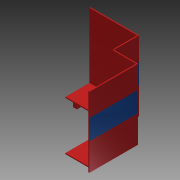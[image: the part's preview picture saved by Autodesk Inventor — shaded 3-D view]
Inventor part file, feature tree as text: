
AUTODESK INVENTOR PART (.ipt)
format: ipt  version: 2014 (Build 180170000, 170)  size: 247,296 bytes
history: native  units: in
note: dims shown in document units (in); Inventor stores cm internally (conversion verified against a paired STEP export)
features: extrude x16, sketch x16
ambient origin geometry x8: Origin, YZ Plane, XZ Plane, XY Plane, X Axis, Y Axis, Z Axis, Center Point
bodies: Solid1 (feature_tree)
feature tree (32):
  extrude  "Extrusion1"  Depth=23.5in
  extrude  "Extrusion2"  Depth=47.5in
  extrude  "Extrusion3"  Depth=64.5in
  extrude  "Extrusion4"  Depth=64.5in
  extrude  "Extrusion5"  Depth=1.0in TaperAngle=0.0deg
  extrude  "Extrusion6"  Depth=1.0in TaperAngle=0.0deg
  extrude  "Extrusion7"  Depth=4.0in
  extrude  "Extrusion8"  Depth=4.0in TaperAngle=0.0deg
  extrude  "Extrusion9"  Depth=4.0in
  extrude  "Extrusion10"  Depth=1.0in TaperAngle=0.0deg
  extrude  "Extrusion11"  Depth=1.0in TaperAngle=0.0deg
  extrude  "Extrusion12"  Depth=1.0in TaperAngle=0.0deg
  sketch  "Sketch13"  dims[d36=0.0in d37=0.0in d38=0.0in d39=0.0in]
  sketch  "Sketch14"  dims[d40=0.0in d41=0.0in d42=0.0in d43=0.0in]
  sketch  "Sketch15"
  sketch  "Sketch16"
  extrude  "Extrusion13"  Depth=0.0in TaperAngle=0.0deg
  extrude  "Extrusion14"  Depth=0.0in TaperAngle=0.0deg
  extrude  "Extrusion15"  [1 undecoded]
  extrude  "Extrusion16"  [1 undecoded]
  sketch  "Sketch1"  dims[d0=47.5in d1=23.5in]
  sketch  "Sketch2"  dims[d2=23.5in d3=47.5in]
  sketch  "Sketch3"  dims[d4=1.0in d5=0.0in d6=64.5in]
  sketch  "Sketch4"  dims[d7=1.0in d8=0.0in d9=64.5in]
  sketch  "Sketch5"  dims[d10=1.0in d11=0.0in d12=1.0in d13=0.0in]
  sketch  "Sketch6"  dims[d14=64.5in d15=1.0in d16=0.0in]
  sketch  "Sketch7"  dims[d17=4.0in d18=4.0in]
  sketch  "Sketch8"  dims[d19=4.0in d20=0.0in d21=0.25in d22=0.0in]
  sketch  "Sketch9"  dims[d23=4.0in d24=4.0in]
  sketch  "Sketch10"  dims[d25=4.0in d26=0.0in d27=1.0in d28=0.0in]
  sketch  "Sketch11"  dims[d29=4.0in d30=1.0in d31=0.0in]
  sketch  "Sketch12"  dims[d32=1.0in d33=0.0in d34=1.0in d35=0.0in]
note: 2 required parameter values undecoded (feature->parameter linkage not recoverable at this tier; creation-order binding heuristic only, values carry confidence <= 0.55)
